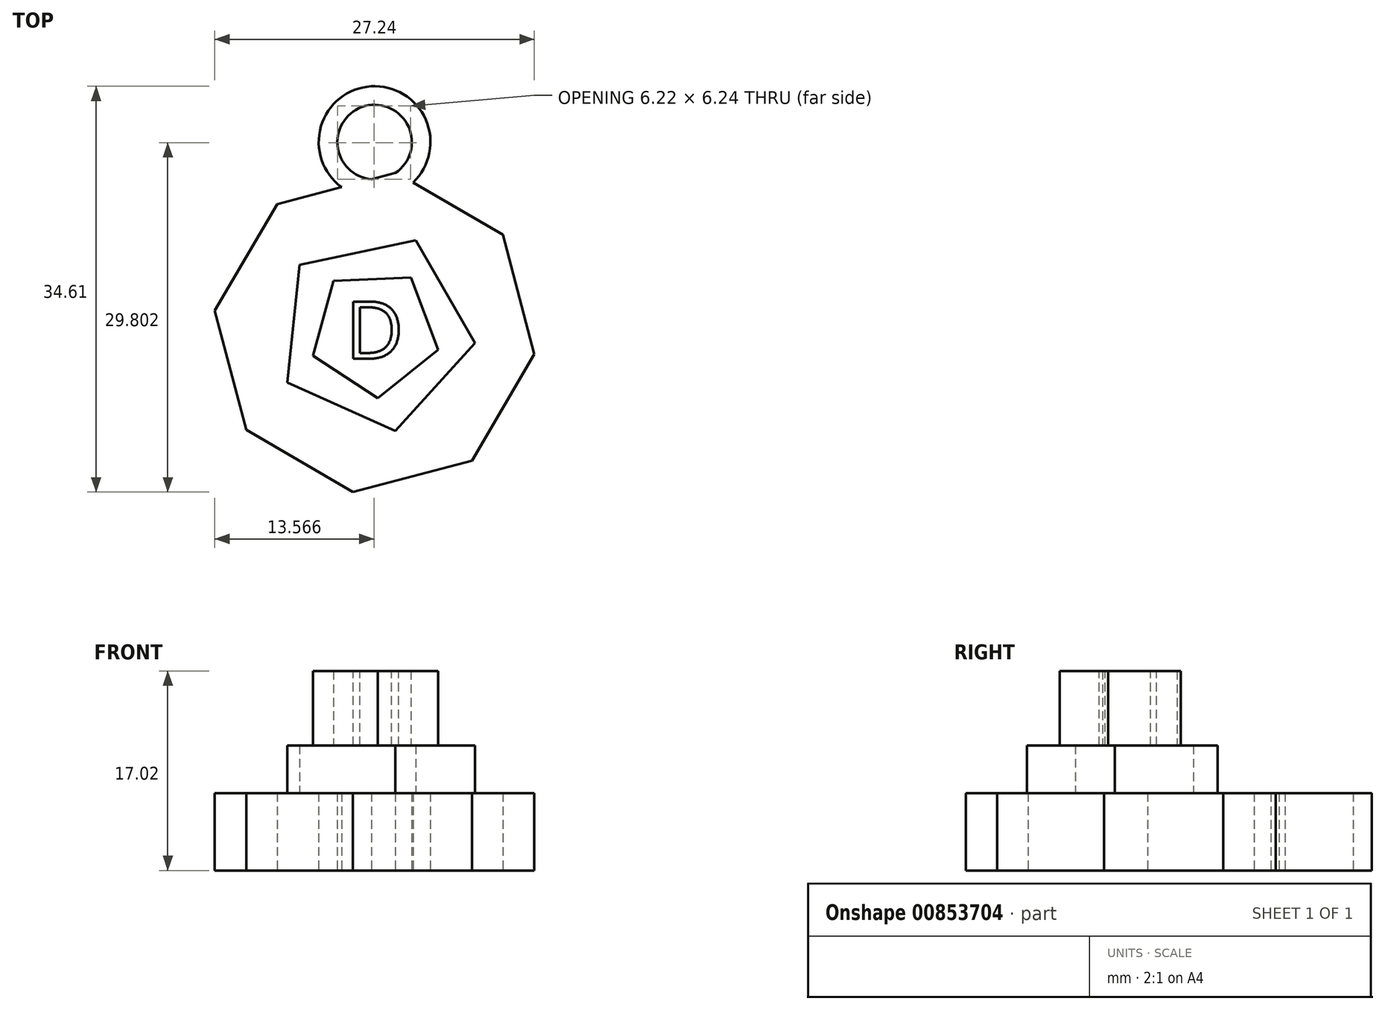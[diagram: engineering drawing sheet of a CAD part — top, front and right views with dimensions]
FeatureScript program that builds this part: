
annotation { "Feature Type Name" : "Feature", "Feature Type Description" : "" }
export const myFeature = defineFeature(function(context is Context, id is Id, definition is map)
    precondition{}
    {
        {
            var Q0;
            Q0=qCreatedBy(makeId("Top.planeOp"),FACE);
            var sketch = newSketch(context, id + "F0", { "sketchPlane" : qUnion([Q0])});
            skArc(sketch, "E0.cCircle", {"start": v(-12.28, -3.23) * mm, "mid": v(10.97, -6.4) * mm, "end": v(-3.23, 12.28) * mm, "construction": true});
            skLineSegment(sketch, "E0.0", {"start": v(13.62, -1.86) * mm, "end": v(8.32, -10.95) * mm});
            skLineSegment(sketch, "E0.1", {"start": v(8.32, -10.95) * mm, "end": v(-1.86, -13.62) * mm});
            skLineSegment(sketch, "E0.2", {"start": v(-1.86, -13.62) * mm, "end": v(-10.95, -8.32) * mm});
            skLineSegment(sketch, "E0.3", {"start": v(-10.95, -8.32) * mm, "end": v(-13.62, 1.86) * mm});
            skLineSegment(sketch, "E0.4", {"start": v(-13.62, 1.86) * mm, "end": v(-8.32, 10.95) * mm});
            skLineSegment(sketch, "E0.5", {"start": v(-8.32, 10.95) * mm, "end": v(1.86, 13.62) * mm});
            skLineSegment(sketch, "E0.6", {"start": v(1.86, 13.62) * mm, "end": v(10.95, 8.32) * mm});
            skLineSegment(sketch, "E0.7", {"start": v(10.95, 8.32) * mm, "end": v(13.62, -1.86) * mm});
            skPoint(sketch, "E0.0.midPoint", {"position": v(10.97, -6.4) * mm});
            skSolve(sketch);
        }
        {
            var Q0;
            Q0=makeQuery(id+"F0.imprint","IMPRINT",FACE,{"disambiguationData":[TD([[makeQuery(id+"F0.imprint","IMPRINT",EDGE,{"derivedFrom":sQuery(id+"F0.wireOp",EDGE,"E0.0")}),-1.0]])]});
            extrude(context, id + "F1", {"entities" : qUnion([Q0]), "depth" : 6.6 * mm, "offsetDistance" : 25.4 * mm});
        }
        {
            var Q0;
            Q0=qCreatedBy(makeId("Top.planeOp"),FACE);
            var sketch = newSketch(context, id + "F2", { "sketchPlane" : qUnion([Q0])});
            skCircle(sketch, "E1.cCircle", {"center": v(0, 0) * mm, "radius": 6.96 * mm, "construction": true});
            skLineSegment(sketch, "E1.0", {"start": v(3.5, 7.85) * mm, "end": v(8.55, -0.91) * mm});
            skLineSegment(sketch, "E1.1", {"start": v(8.55, -0.91) * mm, "end": v(1.78, -8.41) * mm});
            skLineSegment(sketch, "E1.2", {"start": v(1.78, -8.41) * mm, "end": v(-7.45, -4.29) * mm});
            skLineSegment(sketch, "E1.3", {"start": v(-7.45, -4.29) * mm, "end": v(-6.38, 5.76) * mm});
            skLineSegment(sketch, "E1.4", {"start": v(-6.38, 5.76) * mm, "end": v(3.5, 7.85) * mm});
            skPoint(sketch, "E1.0.midPoint", {"position": v(6.03, 3.47) * mm});
            skSolve(sketch);
        }
        {
            var Q0;
            Q0 = qSketchRegion(id + "F2", true);
            extrude(context, id + "F3", {"entities" : qUnion([Q0]), "operationType" : NewBodyOperationType.ADD, "depth" : 10.67 * mm, "offsetDistance" : 25.4 * mm});
        }
        {
            var Q0;
            Q0=makeQuery(id+"F3.opExtrude","CAP_FACE",FACE,{"disambiguationData":[OSD([sQuery(id+"F2.wireOp",EDGE,"E1.0"),sQuery(id+"F2.wireOp",EDGE,"E1.1"),sQuery(id+"F2.wireOp",EDGE,"E1.2"),sQuery(id+"F2.wireOp",EDGE,"E1.3"),sQuery(id+"F2.wireOp",EDGE,"E1.4")])],"isStart":false});
            var sketch = newSketch(context, id + "F4", { "sketchPlane" : qUnion([Q0])});
            skCircle(sketch, "E2.cCircle", {"center": v(0, 0) * mm, "radius": 4.54 * mm, "construction": true});
            skLineSegment(sketch, "E2.0", {"start": v(3.09, 4.7) * mm, "end": v(5.42, -1.49) * mm});
            skLineSegment(sketch, "E2.1", {"start": v(5.42, -1.49) * mm, "end": v(0.26, -5.61) * mm});
            skLineSegment(sketch, "E2.2", {"start": v(0.26, -5.61) * mm, "end": v(-5.26, -1.98) * mm});
            skLineSegment(sketch, "E2.3", {"start": v(-5.26, -1.98) * mm, "end": v(-3.5, 4.39) * mm});
            skLineSegment(sketch, "E2.4", {"start": v(-3.5, 4.39) * mm, "end": v(3.09, 4.7) * mm});
            skPoint(sketch, "E2.0.midPoint", {"position": v(4.25, 1.6) * mm});
            skSolve(sketch);
        }
        {
            var Q0;
            Q0=makeQuery(id+"F4.imprint","IMPRINT",FACE,{"disambiguationData":[TD([[makeQuery(id+"F4.imprint","IMPRINT",EDGE,{"derivedFrom":sQuery(id+"F4.wireOp",EDGE,"E2.0")}),-1.0]])]});
            extrude(context, id + "F5", {"entities" : qUnion([Q0]), "operationType" : NewBodyOperationType.ADD, "depth" : 6.35 * mm, "offsetDistance" : 25.4 * mm});
        }
        {
            var Q0;
            Q0=makeQuery(id+"F5.opExtrude","CAP_FACE",FACE,{"disambiguationData":[OSD([sQuery(id+"F4.wireOp",EDGE,"E2.0"),sQuery(id+"F4.wireOp",EDGE,"E2.1"),sQuery(id+"F4.wireOp",EDGE,"E2.2"),sQuery(id+"F4.wireOp",EDGE,"E2.3"),sQuery(id+"F4.wireOp",EDGE,"E2.4")])],"isStart":false});
            var sketch = newSketch(context, id + "F6", { "sketchPlane" : qUnion([Q0])});
            skText(sketch, "E3", { "text": "D", "fontName": "OpenSans-Regular.ttf"});
            skPoint(sketch, "E3.firstSnap0", {"position": v(-2.5, -3.8) * mm});
            const initialGuessF6  = {"E3": [-0.0025, -0.00225, 1, 0, 0.00491]};
            skSetInitialGuess(sketch, initialGuessF6);
            skSolve(sketch);
        }
        {
            var Q0;
            Q0 = qSketchRegion(id + "F6", true);
            extrude(context, id + "F7", {"entities" : qUnion([Q0]), "operationType" : NewBodyOperationType.REMOVE, "oppositeDirection" : true, "depth" : 6.35 * mm, "offsetDistance" : 25.4 * mm});
        }
        {
            var Q0;
            Q0=qCreatedBy(makeId("Top.planeOp"),FACE);
            var sketch = newSketch(context, id + "F8", { "sketchPlane" : qUnion([Q0])});
            skCircle(sketch, "E4", {"center": v(0, 16.23) * mm, "radius": 4.76 * mm});
            skCircle(sketch, "E5", {"center": v(0, 16.23) * mm, "radius": 3.18 * mm});
            skSolve(sketch);
        }
        {
            var Q0;
            Q0=makeQuery(id+"F8.imprint","IMPRINT",FACE,{"disambiguationData":[TD([[makeQuery(id+"F8.imprint","IMPRINT",EDGE,{"derivedFrom":sQuery(id+"F8.wireOp",EDGE,"E4")}),1.0]])]});
            var Q1;
            Q1=makeQuery(id+"F1.opExtrude","CAP_FACE",FACE,{"disambiguationData":[OSD([sQuery(id+"F0.wireOp",EDGE,"E0.0"),sQuery(id+"F0.wireOp",EDGE,"E0.1"),sQuery(id+"F0.wireOp",EDGE,"E0.2"),sQuery(id+"F0.wireOp",EDGE,"E0.3"),sQuery(id+"F0.wireOp",EDGE,"E0.4"),sQuery(id+"F0.wireOp",EDGE,"E0.5"),sQuery(id+"F0.wireOp",EDGE,"E0.6"),sQuery(id+"F0.wireOp",EDGE,"E0.7")])],"isStart":false});
            extrude(context, id + "F9", {"entities" : qUnion([Q0]), "operationType" : NewBodyOperationType.ADD, "endBound" : BoundingType.UP_TO_SURFACE, "depth" : 25.4 * mm, "endBoundEntityFace" : qUnion([Q1]), "offsetDistance" : 25.4 * mm});
        }
    });
